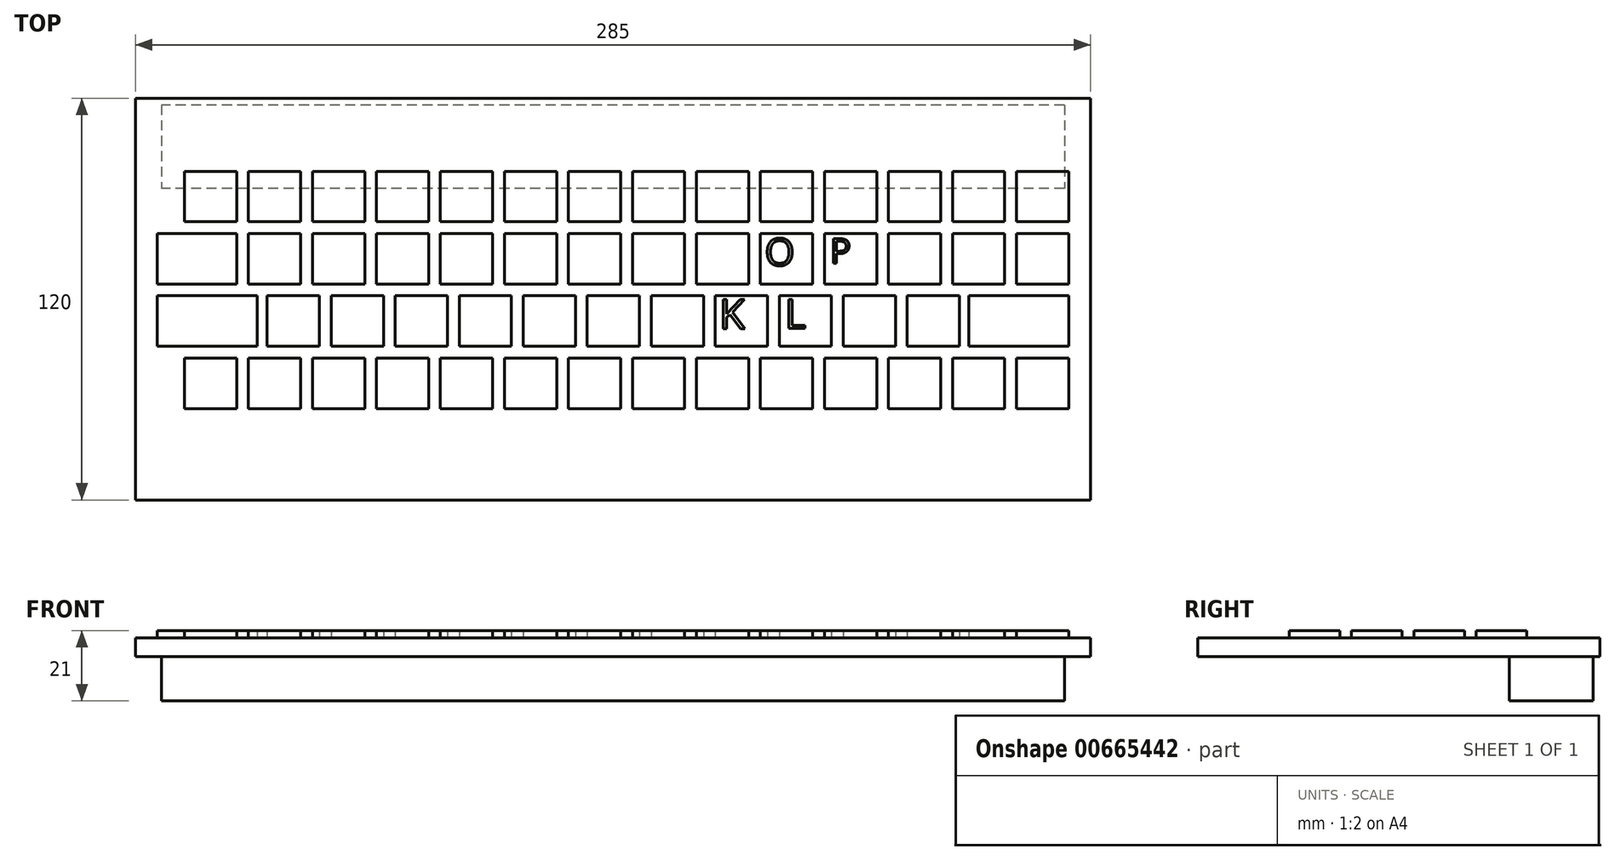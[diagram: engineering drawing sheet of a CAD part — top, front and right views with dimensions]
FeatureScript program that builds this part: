
annotation { "Feature Type Name" : "Feature", "Feature Type Description" : "" }
export const myFeature = defineFeature(function(context is Context, id is Id, definition is map)
    precondition{}
    {
        {
            var Q0;
            Q0=qCreatedBy(makeId("Top.planeOp"),FACE);
            var sketch = newSketch(context, id + "F0", { "sketchPlane" : qUnion([Q0])});
            skLineSegment(sketch, "E0.bottom", {"start": v(142.5, 60) * mm, "end": v(-142.5, 60) * mm});
            skLineSegment(sketch, "E0.top", {"start": v(142.5, -60) * mm, "end": v(-142.5, -60) * mm});
            skLineSegment(sketch, "E0.left", {"start": v(142.5, 60) * mm, "end": v(142.5, -60) * mm});
            skLineSegment(sketch, "E0.right", {"start": v(-142.5, 60) * mm, "end": v(-142.5, -60) * mm});
            skSolve(sketch);
        }
        {
            var Q0;
            Q0=makeQuery(id+"F0.imprint","IMPRINT",FACE,{"disambiguationData":[TD([[makeQuery(id+"F0.imprint","IMPRINT",EDGE,{"derivedFrom":sQuery(id+"F0.wireOp",EDGE,"E0.bottom")}),1.0]])]});
            extrude(context, id + "F1", {"entities" : qUnion([Q0]), "oppositeDirection" : true, "depth" : 5.6 * mm, "offsetDistance" : 25 * mm});
        }
        {
            var Q0;
            Q0=makeQuery(id+"F1.opExtrude","CAP_FACE",FACE,{"disambiguationData":[OSD([sQuery(id+"F0.wireOp",EDGE,"E0.bottom"),sQuery(id+"F0.wireOp",EDGE,"E0.top"),sQuery(id+"F0.wireOp",EDGE,"E0.left"),sQuery(id+"F0.wireOp",EDGE,"E0.right")])],"isStart":true});
            var sketch = newSketch(context, id + "F2", { "sketchPlane" : qUnion([Q0])});
            skLineSegment(sketch, "E1.0.1.0", {"start": v(136, 23.1) * mm, "end": v(120.4, 23.1) * mm});
            skLineSegment(sketch, "E1.0.1.1", {"start": v(120.4, 23.1) * mm, "end": v(120.4, 38.2) * mm});
            skLineSegment(sketch, "E1.0.1.2", {"start": v(136, 23.1) * mm, "end": v(136, 38.2) * mm});
            skPoint(sketch, "E1.0.1.3", {"position": v(128.2, 30.65) * mm});
            skLineSegment(sketch, "E1.0.1.4", {"start": v(136, 38.2) * mm, "end": v(120.4, 38.2) * mm});
            skLineSegment(sketch, "E2.0.1.0", {"start": v(136, 4.5) * mm, "end": v(120.4, 4.5) * mm});
            skLineSegment(sketch, "E2.0.1.1", {"start": v(136, 4.5) * mm, "end": v(136, 19.6) * mm});
            skLineSegment(sketch, "E2.0.1.2", {"start": v(120.4, 4.5) * mm, "end": v(120.4, 19.6) * mm});
            skPoint(sketch, "E2.0.1.3", {"position": v(128.2, 12.05) * mm});
            skLineSegment(sketch, "E2.0.1.4", {"start": v(136, 19.6) * mm, "end": v(120.4, 19.6) * mm});
            skLineSegment(sketch, "E2.0.2.0", {"start": v(136, -14.1) * mm, "end": v(106.2, -14.1) * mm});
            skLineSegment(sketch, "E2.0.2.1", {"start": v(136, -14.1) * mm, "end": v(136, 1) * mm});
            skLineSegment(sketch, "E2.0.2.2", {"start": v(106.2, -14.1) * mm, "end": v(106.2, 1) * mm});
            skPoint(sketch, "E2.0.2.3", {"position": v(115.4, -6.55) * mm});
            skLineSegment(sketch, "E2.0.2.4", {"start": v(136, 1) * mm, "end": v(106.2, 1) * mm});
            skLineSegment(sketch, "E2.0.3.0", {"start": v(136, -32.7) * mm, "end": v(120.4, -32.7) * mm});
            skLineSegment(sketch, "E2.0.3.1", {"start": v(136, -32.7) * mm, "end": v(136, -17.6) * mm});
            skLineSegment(sketch, "E2.0.3.2", {"start": v(120.4, -32.7) * mm, "end": v(120.4, -17.6) * mm});
            skPoint(sketch, "E2.0.3.3", {"position": v(128.2, -25.15) * mm});
            skLineSegment(sketch, "E2.0.3.4", {"start": v(136, -17.6) * mm, "end": v(120.4, -17.6) * mm});
            skLineSegment(sketch, "E2.1.0.0", {"start": v(116.9, 23.1) * mm, "end": v(101.3, 23.1) * mm});
            skLineSegment(sketch, "E2.1.0.1", {"start": v(116.9, 23.1) * mm, "end": v(116.9, 38.2) * mm});
            skLineSegment(sketch, "E2.1.0.2", {"start": v(101.3, 23.1) * mm, "end": v(101.3, 38.2) * mm});
            skPoint(sketch, "E2.1.0.3", {"position": v(109.1, 30.65) * mm});
            skLineSegment(sketch, "E2.1.0.4", {"start": v(116.9, 38.2) * mm, "end": v(101.3, 38.2) * mm});
            skLineSegment(sketch, "E2.1.1.0", {"start": v(116.9, 4.5) * mm, "end": v(101.3, 4.5) * mm});
            skLineSegment(sketch, "E2.1.1.1", {"start": v(116.9, 4.5) * mm, "end": v(116.9, 19.6) * mm});
            skLineSegment(sketch, "E2.1.1.2", {"start": v(101.3, 4.5) * mm, "end": v(101.3, 19.6) * mm});
            skPoint(sketch, "E2.1.1.3", {"position": v(109.1, 12.05) * mm});
            skLineSegment(sketch, "E2.1.1.4", {"start": v(116.9, 19.6) * mm, "end": v(101.3, 19.6) * mm});
            skLineSegment(sketch, "E2.1.3.0", {"start": v(116.9, -32.7) * mm, "end": v(101.3, -32.7) * mm});
            skLineSegment(sketch, "E2.1.3.1", {"start": v(116.9, -32.7) * mm, "end": v(116.9, -17.6) * mm});
            skLineSegment(sketch, "E2.1.3.2", {"start": v(101.3, -32.7) * mm, "end": v(101.3, -17.6) * mm});
            skPoint(sketch, "E2.1.3.3", {"position": v(109.1, -25.15) * mm});
            skLineSegment(sketch, "E2.1.3.4", {"start": v(116.9, -17.6) * mm, "end": v(101.3, -17.6) * mm});
            skLineSegment(sketch, "E2.2.0.0", {"start": v(97.8, 23.1) * mm, "end": v(82.2, 23.1) * mm});
            skLineSegment(sketch, "E2.2.0.1", {"start": v(97.8, 23.1) * mm, "end": v(97.8, 38.2) * mm});
            skLineSegment(sketch, "E2.2.0.2", {"start": v(82.2, 23.1) * mm, "end": v(82.2, 38.2) * mm});
            skPoint(sketch, "E2.2.0.3", {"position": v(90, 30.65) * mm});
            skLineSegment(sketch, "E2.2.0.4", {"start": v(97.8, 38.2) * mm, "end": v(82.2, 38.2) * mm});
            skLineSegment(sketch, "E2.2.1.0", {"start": v(97.8, 4.5) * mm, "end": v(82.2, 4.5) * mm});
            skLineSegment(sketch, "E2.2.1.1", {"start": v(97.8, 4.5) * mm, "end": v(97.8, 19.6) * mm});
            skLineSegment(sketch, "E2.2.1.2", {"start": v(82.2, 4.5) * mm, "end": v(82.2, 19.6) * mm});
            skPoint(sketch, "E2.2.1.3", {"position": v(90, 12.05) * mm});
            skLineSegment(sketch, "E2.2.1.4", {"start": v(97.8, 19.6) * mm, "end": v(82.2, 19.6) * mm});
            skLineSegment(sketch, "E2.2.2.0", {"start": v(103.4, -14.1) * mm, "end": v(87.8, -14.1) * mm});
            skLineSegment(sketch, "E2.2.2.1", {"start": v(103.4, -14.1) * mm, "end": v(103.4, 1) * mm});
            skLineSegment(sketch, "E2.2.2.2", {"start": v(87.8, -14.1) * mm, "end": v(87.8, 1) * mm});
            skPoint(sketch, "E2.2.2.3", {"position": v(95.6, -6.55) * mm});
            skLineSegment(sketch, "E2.2.2.4", {"start": v(103.4, 1) * mm, "end": v(87.8, 1) * mm});
            skLineSegment(sketch, "E2.2.3.0", {"start": v(97.8, -32.7) * mm, "end": v(82.2, -32.7) * mm});
            skLineSegment(sketch, "E2.2.3.1", {"start": v(97.8, -32.7) * mm, "end": v(97.8, -17.6) * mm});
            skLineSegment(sketch, "E2.2.3.2", {"start": v(82.2, -32.7) * mm, "end": v(82.2, -17.6) * mm});
            skPoint(sketch, "E2.2.3.3", {"position": v(90, -25.15) * mm});
            skLineSegment(sketch, "E2.2.3.4", {"start": v(97.8, -17.6) * mm, "end": v(82.2, -17.6) * mm});
            skLineSegment(sketch, "E2.3.0.0", {"start": v(78.7, 23.1) * mm, "end": v(63.1, 23.1) * mm});
            skLineSegment(sketch, "E2.3.0.1", {"start": v(78.7, 23.1) * mm, "end": v(78.7, 38.2) * mm});
            skLineSegment(sketch, "E2.3.0.2", {"start": v(63.1, 23.1) * mm, "end": v(63.1, 38.2) * mm});
            skPoint(sketch, "E2.3.0.3", {"position": v(70.9, 30.65) * mm});
            skLineSegment(sketch, "E2.3.0.4", {"start": v(78.7, 38.2) * mm, "end": v(63.1, 38.2) * mm});
            skLineSegment(sketch, "E2.3.1.0", {"start": v(78.7, 4.5) * mm, "end": v(63.1, 4.5) * mm});
            skLineSegment(sketch, "E2.3.1.1", {"start": v(78.7, 4.5) * mm, "end": v(78.7, 19.6) * mm});
            skLineSegment(sketch, "E2.3.1.2", {"start": v(63.1, 4.5) * mm, "end": v(63.1, 19.6) * mm});
            skPoint(sketch, "E2.3.1.3", {"position": v(70.9, 12.05) * mm});
            skLineSegment(sketch, "E2.3.1.4", {"start": v(78.7, 19.6) * mm, "end": v(63.1, 19.6) * mm});
            skLineSegment(sketch, "E2.3.2.0", {"start": v(84.3, -14.1) * mm, "end": v(68.7, -14.1) * mm});
            skLineSegment(sketch, "E2.3.2.1", {"start": v(84.3, -14.1) * mm, "end": v(84.3, 1) * mm});
            skLineSegment(sketch, "E2.3.2.2", {"start": v(68.7, -14.1) * mm, "end": v(68.7, 1) * mm});
            skPoint(sketch, "E2.3.2.3", {"position": v(76.5, -6.55) * mm});
            skLineSegment(sketch, "E2.3.2.4", {"start": v(84.3, 1) * mm, "end": v(68.7, 1) * mm});
            skLineSegment(sketch, "E2.3.3.0", {"start": v(78.7, -32.7) * mm, "end": v(63.1, -32.7) * mm});
            skLineSegment(sketch, "E2.3.3.1", {"start": v(78.7, -32.7) * mm, "end": v(78.7, -17.6) * mm});
            skLineSegment(sketch, "E2.3.3.2", {"start": v(63.1, -32.7) * mm, "end": v(63.1, -17.6) * mm});
            skPoint(sketch, "E2.3.3.3", {"position": v(70.9, -25.15) * mm});
            skLineSegment(sketch, "E2.3.3.4", {"start": v(78.7, -17.6) * mm, "end": v(63.1, -17.6) * mm});
            skLineSegment(sketch, "E2.4.0.0", {"start": v(59.6, 23.1) * mm, "end": v(44, 23.1) * mm});
            skLineSegment(sketch, "E2.4.0.1", {"start": v(59.6, 23.1) * mm, "end": v(59.6, 38.2) * mm});
            skLineSegment(sketch, "E2.4.0.2", {"start": v(44, 23.1) * mm, "end": v(44, 38.2) * mm});
            skPoint(sketch, "E2.4.0.3", {"position": v(51.8, 30.65) * mm});
            skLineSegment(sketch, "E2.4.0.4", {"start": v(59.6, 38.2) * mm, "end": v(44, 38.2) * mm});
            skLineSegment(sketch, "E2.4.1.0", {"start": v(59.6, 4.5) * mm, "end": v(44, 4.5) * mm});
            skLineSegment(sketch, "E2.4.1.1", {"start": v(59.6, 4.5) * mm, "end": v(59.6, 19.6) * mm});
            skLineSegment(sketch, "E2.4.1.2", {"start": v(44, 4.5) * mm, "end": v(44, 19.6) * mm});
            skPoint(sketch, "E2.4.1.3", {"position": v(51.8, 12.05) * mm});
            skLineSegment(sketch, "E2.4.1.4", {"start": v(59.6, 19.6) * mm, "end": v(44, 19.6) * mm});
            skLineSegment(sketch, "E2.4.2.0", {"start": v(65.2, -14.1) * mm, "end": v(49.6, -14.1) * mm});
            skLineSegment(sketch, "E2.4.2.1", {"start": v(65.2, -14.1) * mm, "end": v(65.2, 1) * mm});
            skLineSegment(sketch, "E2.4.2.2", {"start": v(49.6, -14.1) * mm, "end": v(49.6, 1) * mm});
            skPoint(sketch, "E2.4.2.3", {"position": v(57.4, -6.55) * mm});
            skLineSegment(sketch, "E2.4.2.4", {"start": v(65.2, 1) * mm, "end": v(49.6, 1) * mm});
            skLineSegment(sketch, "E2.4.3.0", {"start": v(59.6, -32.7) * mm, "end": v(44, -32.7) * mm});
            skLineSegment(sketch, "E2.4.3.1", {"start": v(59.6, -32.7) * mm, "end": v(59.6, -17.6) * mm});
            skLineSegment(sketch, "E2.4.3.2", {"start": v(44, -32.7) * mm, "end": v(44, -17.6) * mm});
            skPoint(sketch, "E2.4.3.3", {"position": v(51.8, -25.15) * mm});
            skLineSegment(sketch, "E2.4.3.4", {"start": v(59.6, -17.6) * mm, "end": v(44, -17.6) * mm});
            skLineSegment(sketch, "E2.5.0.0", {"start": v(40.5, 23.1) * mm, "end": v(24.9, 23.1) * mm});
            skLineSegment(sketch, "E2.5.0.1", {"start": v(40.5, 23.1) * mm, "end": v(40.5, 38.2) * mm});
            skLineSegment(sketch, "E2.5.0.2", {"start": v(24.9, 23.1) * mm, "end": v(24.9, 38.2) * mm});
            skPoint(sketch, "E2.5.0.3", {"position": v(32.7, 30.65) * mm});
            skLineSegment(sketch, "E2.5.0.4", {"start": v(40.5, 38.2) * mm, "end": v(24.9, 38.2) * mm});
            skLineSegment(sketch, "E2.5.1.0", {"start": v(40.5, 4.5) * mm, "end": v(24.9, 4.5) * mm});
            skLineSegment(sketch, "E2.5.1.1", {"start": v(40.5, 4.5) * mm, "end": v(40.5, 19.6) * mm});
            skLineSegment(sketch, "E2.5.1.2", {"start": v(24.9, 4.5) * mm, "end": v(24.9, 19.6) * mm});
            skPoint(sketch, "E2.5.1.3", {"position": v(32.7, 12.05) * mm});
            skLineSegment(sketch, "E2.5.1.4", {"start": v(40.5, 19.6) * mm, "end": v(24.9, 19.6) * mm});
            skLineSegment(sketch, "E2.5.2.0", {"start": v(46.1, -14.1) * mm, "end": v(30.5, -14.1) * mm});
            skLineSegment(sketch, "E2.5.2.1", {"start": v(46.1, -14.1) * mm, "end": v(46.1, 1) * mm});
            skLineSegment(sketch, "E2.5.2.2", {"start": v(30.5, -14.1) * mm, "end": v(30.5, 1) * mm});
            skPoint(sketch, "E2.5.2.3", {"position": v(38.3, -6.55) * mm});
            skLineSegment(sketch, "E2.5.2.4", {"start": v(46.1, 1) * mm, "end": v(30.5, 1) * mm});
            skLineSegment(sketch, "E2.5.3.0", {"start": v(40.5, -32.7) * mm, "end": v(24.9, -32.7) * mm});
            skLineSegment(sketch, "E2.5.3.1", {"start": v(40.5, -32.7) * mm, "end": v(40.5, -17.6) * mm});
            skLineSegment(sketch, "E2.5.3.2", {"start": v(24.9, -32.7) * mm, "end": v(24.9, -17.6) * mm});
            skPoint(sketch, "E2.5.3.3", {"position": v(32.7, -25.15) * mm});
            skLineSegment(sketch, "E2.5.3.4", {"start": v(40.5, -17.6) * mm, "end": v(24.9, -17.6) * mm});
            skLineSegment(sketch, "E2.6.0.0", {"start": v(21.4, 23.1) * mm, "end": v(5.8, 23.1) * mm});
            skLineSegment(sketch, "E2.6.0.1", {"start": v(21.4, 23.1) * mm, "end": v(21.4, 38.2) * mm});
            skLineSegment(sketch, "E2.6.0.2", {"start": v(5.8, 23.1) * mm, "end": v(5.8, 38.2) * mm});
            skPoint(sketch, "E2.6.0.3", {"position": v(13.6, 30.65) * mm});
            skLineSegment(sketch, "E2.6.0.4", {"start": v(21.4, 38.2) * mm, "end": v(5.8, 38.2) * mm});
            skLineSegment(sketch, "E2.6.1.0", {"start": v(21.4, 4.5) * mm, "end": v(5.8, 4.5) * mm});
            skLineSegment(sketch, "E2.6.1.1", {"start": v(21.4, 4.5) * mm, "end": v(21.4, 19.6) * mm});
            skLineSegment(sketch, "E2.6.1.2", {"start": v(5.8, 4.5) * mm, "end": v(5.8, 19.6) * mm});
            skPoint(sketch, "E2.6.1.3", {"position": v(13.6, 12.05) * mm});
            skLineSegment(sketch, "E2.6.1.4", {"start": v(21.4, 19.6) * mm, "end": v(5.8, 19.6) * mm});
            skLineSegment(sketch, "E2.6.2.0", {"start": v(27, -14.1) * mm, "end": v(11.4, -14.1) * mm});
            skLineSegment(sketch, "E2.6.2.1", {"start": v(27, -14.1) * mm, "end": v(27, 1) * mm});
            skLineSegment(sketch, "E2.6.2.2", {"start": v(11.4, -14.1) * mm, "end": v(11.4, 1) * mm});
            skPoint(sketch, "E2.6.2.3", {"position": v(19.2, -6.55) * mm});
            skLineSegment(sketch, "E2.6.2.4", {"start": v(27, 1) * mm, "end": v(11.4, 1) * mm});
            skLineSegment(sketch, "E2.6.3.0", {"start": v(21.4, -32.7) * mm, "end": v(5.8, -32.7) * mm});
            skLineSegment(sketch, "E2.6.3.1", {"start": v(21.4, -32.7) * mm, "end": v(21.4, -17.6) * mm});
            skLineSegment(sketch, "E2.6.3.2", {"start": v(5.8, -32.7) * mm, "end": v(5.8, -17.6) * mm});
            skPoint(sketch, "E2.6.3.3", {"position": v(13.6, -25.15) * mm});
            skLineSegment(sketch, "E2.6.3.4", {"start": v(21.4, -17.6) * mm, "end": v(5.8, -17.6) * mm});
            skLineSegment(sketch, "E2.7.0.0", {"start": v(2.3, 23.1) * mm, "end": v(-13.3, 23.1) * mm});
            skLineSegment(sketch, "E2.7.0.1", {"start": v(2.3, 23.1) * mm, "end": v(2.3, 38.2) * mm});
            skLineSegment(sketch, "E2.7.0.2", {"start": v(-13.3, 23.1) * mm, "end": v(-13.3, 38.2) * mm});
            skPoint(sketch, "E2.7.0.3", {"position": v(-5.5, 30.65) * mm});
            skLineSegment(sketch, "E2.7.0.4", {"start": v(2.3, 38.2) * mm, "end": v(-13.3, 38.2) * mm});
            skLineSegment(sketch, "E2.7.1.0", {"start": v(2.3, 4.5) * mm, "end": v(-13.3, 4.5) * mm});
            skLineSegment(sketch, "E2.7.1.1", {"start": v(2.3, 4.5) * mm, "end": v(2.3, 19.6) * mm});
            skLineSegment(sketch, "E2.7.1.2", {"start": v(-13.3, 4.5) * mm, "end": v(-13.3, 19.6) * mm});
            skPoint(sketch, "E2.7.1.3", {"position": v(-5.5, 12.05) * mm});
            skLineSegment(sketch, "E2.7.1.4", {"start": v(2.3, 19.6) * mm, "end": v(-13.3, 19.6) * mm});
            skLineSegment(sketch, "E2.7.2.0", {"start": v(7.9, -14.1) * mm, "end": v(-7.7, -14.1) * mm});
            skLineSegment(sketch, "E2.7.2.1", {"start": v(7.9, -14.1) * mm, "end": v(7.9, 1) * mm});
            skLineSegment(sketch, "E2.7.2.2", {"start": v(-7.7, -14.1) * mm, "end": v(-7.7, 1) * mm});
            skPoint(sketch, "E2.7.2.3", {"position": v(0.1, -6.55) * mm});
            skLineSegment(sketch, "E2.7.2.4", {"start": v(7.9, 1) * mm, "end": v(-7.7, 1) * mm});
            skLineSegment(sketch, "E2.7.3.0", {"start": v(2.3, -32.7) * mm, "end": v(-13.3, -32.7) * mm});
            skLineSegment(sketch, "E2.7.3.1", {"start": v(2.3, -32.7) * mm, "end": v(2.3, -17.6) * mm});
            skLineSegment(sketch, "E2.7.3.2", {"start": v(-13.3, -32.7) * mm, "end": v(-13.3, -17.6) * mm});
            skPoint(sketch, "E2.7.3.3", {"position": v(-5.5, -25.15) * mm});
            skLineSegment(sketch, "E2.7.3.4", {"start": v(2.3, -17.6) * mm, "end": v(-13.3, -17.6) * mm});
            skLineSegment(sketch, "E2.8.0.0", {"start": v(-16.8, 23.1) * mm, "end": v(-32.4, 23.1) * mm});
            skLineSegment(sketch, "E2.8.0.1", {"start": v(-16.8, 23.1) * mm, "end": v(-16.8, 38.2) * mm});
            skLineSegment(sketch, "E2.8.0.2", {"start": v(-32.4, 23.1) * mm, "end": v(-32.4, 38.2) * mm});
            skPoint(sketch, "E2.8.0.3", {"position": v(-24.6, 30.65) * mm});
            skLineSegment(sketch, "E2.8.0.4", {"start": v(-16.8, 38.2) * mm, "end": v(-32.4, 38.2) * mm});
            skLineSegment(sketch, "E2.8.1.0", {"start": v(-16.8, 4.5) * mm, "end": v(-32.4, 4.5) * mm});
            skLineSegment(sketch, "E2.8.1.1", {"start": v(-16.8, 4.5) * mm, "end": v(-16.8, 19.6) * mm});
            skLineSegment(sketch, "E2.8.1.2", {"start": v(-32.4, 4.5) * mm, "end": v(-32.4, 19.6) * mm});
            skPoint(sketch, "E2.8.1.3", {"position": v(-24.6, 12.05) * mm});
            skLineSegment(sketch, "E2.8.1.4", {"start": v(-16.8, 19.6) * mm, "end": v(-32.4, 19.6) * mm});
            skLineSegment(sketch, "E2.8.2.0", {"start": v(-11.2, -14.1) * mm, "end": v(-26.8, -14.1) * mm});
            skLineSegment(sketch, "E2.8.2.1", {"start": v(-11.2, -14.1) * mm, "end": v(-11.2, 1) * mm});
            skLineSegment(sketch, "E2.8.2.2", {"start": v(-26.8, -14.1) * mm, "end": v(-26.8, 1) * mm});
            skPoint(sketch, "E2.8.2.3", {"position": v(-19, -6.55) * mm});
            skLineSegment(sketch, "E2.8.2.4", {"start": v(-11.2, 1) * mm, "end": v(-26.8, 1) * mm});
            skLineSegment(sketch, "E2.8.3.0", {"start": v(-16.8, -32.7) * mm, "end": v(-32.4, -32.7) * mm});
            skLineSegment(sketch, "E2.8.3.1", {"start": v(-16.8, -32.7) * mm, "end": v(-16.8, -17.6) * mm});
            skLineSegment(sketch, "E2.8.3.2", {"start": v(-32.4, -32.7) * mm, "end": v(-32.4, -17.6) * mm});
            skPoint(sketch, "E2.8.3.3", {"position": v(-24.6, -25.15) * mm});
            skLineSegment(sketch, "E2.8.3.4", {"start": v(-16.8, -17.6) * mm, "end": v(-32.4, -17.6) * mm});
            skLineSegment(sketch, "E2.9.0.0", {"start": v(-35.9, 23.1) * mm, "end": v(-51.5, 23.1) * mm});
            skLineSegment(sketch, "E2.9.0.1", {"start": v(-35.9, 23.1) * mm, "end": v(-35.9, 38.2) * mm});
            skLineSegment(sketch, "E2.9.0.2", {"start": v(-51.5, 23.1) * mm, "end": v(-51.5, 38.2) * mm});
            skPoint(sketch, "E2.9.0.3", {"position": v(-43.7, 30.65) * mm});
            skLineSegment(sketch, "E2.9.0.4", {"start": v(-35.9, 38.2) * mm, "end": v(-51.5, 38.2) * mm});
            skLineSegment(sketch, "E2.9.1.0", {"start": v(-35.9, 4.5) * mm, "end": v(-51.5, 4.5) * mm});
            skLineSegment(sketch, "E2.9.1.1", {"start": v(-35.9, 4.5) * mm, "end": v(-35.9, 19.6) * mm});
            skLineSegment(sketch, "E2.9.1.2", {"start": v(-51.5, 4.5) * mm, "end": v(-51.5, 19.6) * mm});
            skPoint(sketch, "E2.9.1.3", {"position": v(-43.7, 12.05) * mm});
            skLineSegment(sketch, "E2.9.1.4", {"start": v(-35.9, 19.6) * mm, "end": v(-51.5, 19.6) * mm});
            skLineSegment(sketch, "E2.9.2.0", {"start": v(-30.3, -14.1) * mm, "end": v(-45.9, -14.1) * mm});
            skLineSegment(sketch, "E2.9.2.1", {"start": v(-30.3, -14.1) * mm, "end": v(-30.3, 1) * mm});
            skLineSegment(sketch, "E2.9.2.2", {"start": v(-45.9, -14.1) * mm, "end": v(-45.9, 1) * mm});
            skPoint(sketch, "E2.9.2.3", {"position": v(-38.1, -6.55) * mm});
            skLineSegment(sketch, "E2.9.2.4", {"start": v(-30.3, 1) * mm, "end": v(-45.9, 1) * mm});
            skLineSegment(sketch, "E2.9.3.0", {"start": v(-35.9, -32.7) * mm, "end": v(-51.5, -32.7) * mm});
            skLineSegment(sketch, "E2.9.3.1", {"start": v(-35.9, -32.7) * mm, "end": v(-35.9, -17.6) * mm});
            skLineSegment(sketch, "E2.9.3.2", {"start": v(-51.5, -32.7) * mm, "end": v(-51.5, -17.6) * mm});
            skPoint(sketch, "E2.9.3.3", {"position": v(-43.7, -25.15) * mm});
            skLineSegment(sketch, "E2.9.3.4", {"start": v(-35.9, -17.6) * mm, "end": v(-51.5, -17.6) * mm});
            skLineSegment(sketch, "E2.10.0.0", {"start": v(-55, 23.1) * mm, "end": v(-70.6, 23.1) * mm});
            skLineSegment(sketch, "E2.10.0.1", {"start": v(-55, 23.1) * mm, "end": v(-55, 38.2) * mm});
            skLineSegment(sketch, "E2.10.0.2", {"start": v(-70.6, 23.1) * mm, "end": v(-70.6, 38.2) * mm});
            skPoint(sketch, "E2.10.0.3", {"position": v(-62.8, 30.65) * mm});
            skLineSegment(sketch, "E2.10.0.4", {"start": v(-55, 38.2) * mm, "end": v(-70.6, 38.2) * mm});
            skLineSegment(sketch, "E2.10.1.0", {"start": v(-55, 4.5) * mm, "end": v(-70.6, 4.5) * mm});
            skLineSegment(sketch, "E2.10.1.1", {"start": v(-55, 4.5) * mm, "end": v(-55, 19.6) * mm});
            skLineSegment(sketch, "E2.10.1.2", {"start": v(-70.6, 4.5) * mm, "end": v(-70.6, 19.6) * mm});
            skPoint(sketch, "E2.10.1.3", {"position": v(-62.8, 12.05) * mm});
            skLineSegment(sketch, "E2.10.1.4", {"start": v(-55, 19.6) * mm, "end": v(-70.6, 19.6) * mm});
            skLineSegment(sketch, "E2.10.2.0", {"start": v(-49.4, -14.1) * mm, "end": v(-65, -14.1) * mm});
            skLineSegment(sketch, "E2.10.2.1", {"start": v(-49.4, -14.1) * mm, "end": v(-49.4, 1) * mm});
            skLineSegment(sketch, "E2.10.2.2", {"start": v(-65, -14.1) * mm, "end": v(-65, 1) * mm});
            skPoint(sketch, "E2.10.2.3", {"position": v(-57.2, -6.55) * mm});
            skLineSegment(sketch, "E2.10.2.4", {"start": v(-49.4, 1) * mm, "end": v(-65, 1) * mm});
            skLineSegment(sketch, "E2.10.3.0", {"start": v(-55, -32.7) * mm, "end": v(-70.6, -32.7) * mm});
            skLineSegment(sketch, "E2.10.3.1", {"start": v(-55, -32.7) * mm, "end": v(-55, -17.6) * mm});
            skLineSegment(sketch, "E2.10.3.2", {"start": v(-70.6, -32.7) * mm, "end": v(-70.6, -17.6) * mm});
            skPoint(sketch, "E2.10.3.3", {"position": v(-62.8, -25.15) * mm});
            skLineSegment(sketch, "E2.10.3.4", {"start": v(-55, -17.6) * mm, "end": v(-70.6, -17.6) * mm});
            skLineSegment(sketch, "E2.11.0.0", {"start": v(-74.1, 23.1) * mm, "end": v(-89.7, 23.1) * mm});
            skLineSegment(sketch, "E2.11.0.1", {"start": v(-74.1, 23.1) * mm, "end": v(-74.1, 38.2) * mm});
            skLineSegment(sketch, "E2.11.0.2", {"start": v(-89.7, 23.1) * mm, "end": v(-89.7, 38.2) * mm});
            skPoint(sketch, "E2.11.0.3", {"position": v(-81.9, 30.65) * mm});
            skLineSegment(sketch, "E2.11.0.4", {"start": v(-74.1, 38.2) * mm, "end": v(-89.7, 38.2) * mm});
            skLineSegment(sketch, "E2.11.1.0", {"start": v(-74.1, 4.5) * mm, "end": v(-89.7, 4.5) * mm});
            skLineSegment(sketch, "E2.11.1.1", {"start": v(-74.1, 4.5) * mm, "end": v(-74.1, 19.6) * mm});
            skLineSegment(sketch, "E2.11.1.2", {"start": v(-89.7, 4.5) * mm, "end": v(-89.7, 19.6) * mm});
            skPoint(sketch, "E2.11.1.3", {"position": v(-81.9, 12.05) * mm});
            skLineSegment(sketch, "E2.11.1.4", {"start": v(-74.1, 19.6) * mm, "end": v(-89.7, 19.6) * mm});
            skLineSegment(sketch, "E2.11.2.0", {"start": v(-68.5, -14.1) * mm, "end": v(-84.1, -14.1) * mm});
            skLineSegment(sketch, "E2.11.2.1", {"start": v(-68.5, -14.1) * mm, "end": v(-68.5, 1) * mm});
            skLineSegment(sketch, "E2.11.2.2", {"start": v(-84.1, -14.1) * mm, "end": v(-84.1, 1) * mm});
            skPoint(sketch, "E2.11.2.3", {"position": v(-76.3, -6.55) * mm});
            skLineSegment(sketch, "E2.11.2.4", {"start": v(-68.5, 1) * mm, "end": v(-84.1, 1) * mm});
            skLineSegment(sketch, "E2.11.3.0", {"start": v(-74.1, -32.7) * mm, "end": v(-89.7, -32.7) * mm});
            skLineSegment(sketch, "E2.11.3.1", {"start": v(-74.1, -32.7) * mm, "end": v(-74.1, -17.6) * mm});
            skLineSegment(sketch, "E2.11.3.2", {"start": v(-89.7, -32.7) * mm, "end": v(-89.7, -17.6) * mm});
            skPoint(sketch, "E2.11.3.3", {"position": v(-81.9, -25.15) * mm});
            skLineSegment(sketch, "E2.11.3.4", {"start": v(-74.1, -17.6) * mm, "end": v(-89.7, -17.6) * mm});
            skLineSegment(sketch, "E2.12.0.0", {"start": v(-93.2, 23.1) * mm, "end": v(-108.8, 23.1) * mm});
            skLineSegment(sketch, "E2.12.0.1", {"start": v(-93.2, 23.1) * mm, "end": v(-93.2, 38.2) * mm});
            skLineSegment(sketch, "E2.12.0.2", {"start": v(-108.8, 23.1) * mm, "end": v(-108.8, 38.2) * mm});
            skPoint(sketch, "E2.12.0.3", {"position": v(-101, 30.65) * mm});
            skLineSegment(sketch, "E2.12.0.4", {"start": v(-93.2, 38.2) * mm, "end": v(-108.8, 38.2) * mm});
            skLineSegment(sketch, "E2.12.1.0", {"start": v(-93.2, 4.5) * mm, "end": v(-108.8, 4.5) * mm});
            skLineSegment(sketch, "E2.12.1.1", {"start": v(-93.2, 4.5) * mm, "end": v(-93.2, 19.6) * mm});
            skLineSegment(sketch, "E2.12.1.2", {"start": v(-108.8, 4.5) * mm, "end": v(-108.8, 19.6) * mm});
            skPoint(sketch, "E2.12.1.3", {"position": v(-101, 12.05) * mm});
            skLineSegment(sketch, "E2.12.1.4", {"start": v(-93.2, 19.6) * mm, "end": v(-108.8, 19.6) * mm});
            skLineSegment(sketch, "E2.12.2.0", {"start": v(-87.6, -14.1) * mm, "end": v(-103.2, -14.1) * mm});
            skLineSegment(sketch, "E2.12.2.1", {"start": v(-87.6, -14.1) * mm, "end": v(-87.6, 1) * mm});
            skLineSegment(sketch, "E2.12.2.2", {"start": v(-103.2, -14.1) * mm, "end": v(-103.2, 1) * mm});
            skPoint(sketch, "E2.12.2.3", {"position": v(-95.4, -6.55) * mm});
            skLineSegment(sketch, "E2.12.2.4", {"start": v(-87.6, 1) * mm, "end": v(-103.2, 1) * mm});
            skLineSegment(sketch, "E2.12.3.0", {"start": v(-93.2, -32.7) * mm, "end": v(-108.8, -32.7) * mm});
            skLineSegment(sketch, "E2.12.3.1", {"start": v(-93.2, -32.7) * mm, "end": v(-93.2, -17.6) * mm});
            skLineSegment(sketch, "E2.12.3.2", {"start": v(-108.8, -32.7) * mm, "end": v(-108.8, -17.6) * mm});
            skPoint(sketch, "E2.12.3.3", {"position": v(-101, -25.15) * mm});
            skLineSegment(sketch, "E2.12.3.4", {"start": v(-93.2, -17.6) * mm, "end": v(-108.8, -17.6) * mm});
            skLineSegment(sketch, "E2.13.0.0", {"start": v(-112.3, 23.1) * mm, "end": v(-127.9, 23.1) * mm});
            skLineSegment(sketch, "E2.13.0.1", {"start": v(-112.3, 23.1) * mm, "end": v(-112.3, 38.2) * mm});
            skLineSegment(sketch, "E2.13.0.2", {"start": v(-127.9, 23.1) * mm, "end": v(-127.9, 38.2) * mm});
            skPoint(sketch, "E2.13.0.3", {"position": v(-120.1, 30.65) * mm});
            skLineSegment(sketch, "E2.13.0.4", {"start": v(-112.3, 38.2) * mm, "end": v(-127.9, 38.2) * mm});
            skLineSegment(sketch, "E2.13.1.0", {"start": v(-112.3, 4.5) * mm, "end": v(-136, 4.5) * mm});
            skLineSegment(sketch, "E2.13.1.1", {"start": v(-112.3, 4.5) * mm, "end": v(-112.3, 19.6) * mm});
            skLineSegment(sketch, "E2.13.1.2", {"start": v(-136, 4.5) * mm, "end": v(-136, 19.6) * mm});
            skPoint(sketch, "E2.13.1.3", {"position": v(-127.7, 12.05) * mm});
            skLineSegment(sketch, "E2.13.1.4", {"start": v(-112.3, 19.6) * mm, "end": v(-136, 19.6) * mm});
            skLineSegment(sketch, "E2.13.2.0", {"start": v(-106.2, -14.1) * mm, "end": v(-136, -14.1) * mm});
            skLineSegment(sketch, "E2.13.2.1", {"start": v(-106.2, -14.1) * mm, "end": v(-106.2, 1) * mm});
            skLineSegment(sketch, "E2.13.2.2", {"start": v(-136, -14.1) * mm, "end": v(-136, 1) * mm});
            skPoint(sketch, "E2.13.2.3", {"position": v(-120.1, -6.55) * mm});
            skLineSegment(sketch, "E2.13.2.4", {"start": v(-106.2, 1) * mm, "end": v(-136, 1) * mm});
            skLineSegment(sketch, "E2.13.3.0", {"start": v(-112.3, -32.7) * mm, "end": v(-127.9, -32.7) * mm});
            skLineSegment(sketch, "E2.13.3.1", {"start": v(-112.3, -32.7) * mm, "end": v(-112.3, -17.6) * mm});
            skLineSegment(sketch, "E2.13.3.2", {"start": v(-127.9, -32.7) * mm, "end": v(-127.9, -17.6) * mm});
            skPoint(sketch, "E2.13.3.3", {"position": v(-120.1, -25.15) * mm});
            skLineSegment(sketch, "E2.13.3.4", {"start": v(-112.3, -17.6) * mm, "end": v(-127.9, -17.6) * mm});
            skLineSegment(sketch, "E2.direction1", {"start": v(120.4, 23.1) * mm, "end": v(101.3, 23.1) * mm, "construction": true});
            skLineSegment(sketch, "E2.direction2", {"start": v(120.4, 23.1) * mm, "end": v(120.4, 4.5) * mm, "construction": true});
            skSolve(sketch);
        }
        {
            var Q0;
            Q0=makeQuery(id+"F2.imprint","IMPRINT",FACE,{"disambiguationData":[TD([[makeQuery(id+"F2.imprint","IMPRINT",EDGE,{"derivedFrom":sQuery(id+"F2.wireOp",EDGE,"E2.13.0.0")}),-1.0]])]});
            var Q1;
            Q1=makeQuery(id+"F2.imprint","IMPRINT",FACE,{"disambiguationData":[TD([[makeQuery(id+"F2.imprint","IMPRINT",EDGE,{"derivedFrom":sQuery(id+"F2.wireOp",EDGE,"E2.13.1.0")}),-1.0]])]});
            var Q2;
            Q2=makeQuery(id+"F2.imprint","IMPRINT",FACE,{"disambiguationData":[TD([[makeQuery(id+"F2.imprint","IMPRINT",EDGE,{"derivedFrom":sQuery(id+"F2.wireOp",EDGE,"E2.13.2.0")}),-1.0]])]});
            var Q3;
            Q3=makeQuery(id+"F2.imprint","IMPRINT",FACE,{"disambiguationData":[TD([[makeQuery(id+"F2.imprint","IMPRINT",EDGE,{"derivedFrom":sQuery(id+"F2.wireOp",EDGE,"E2.12.1.0")}),-1.0]])]});
            var Q4;
            Q4=makeQuery(id+"F2.imprint","IMPRINT",FACE,{"disambiguationData":[TD([[makeQuery(id+"F2.imprint","IMPRINT",EDGE,{"derivedFrom":sQuery(id+"F2.wireOp",EDGE,"E2.12.0.0")}),-1.0]])]});
            var Q5;
            Q5=makeQuery(id+"F2.imprint","IMPRINT",FACE,{"disambiguationData":[TD([[makeQuery(id+"F2.imprint","IMPRINT",EDGE,{"derivedFrom":sQuery(id+"F2.wireOp",EDGE,"E2.9.2.0")}),-1.0]])]});
            var Q6;
            Q6=makeQuery(id+"F2.imprint","IMPRINT",FACE,{"disambiguationData":[TD([[makeQuery(id+"F2.imprint","IMPRINT",EDGE,{"derivedFrom":sQuery(id+"F2.wireOp",EDGE,"E2.5.2.0")}),-1.0]])]});
            var Q7;
            Q7=makeQuery(id+"F2.imprint","IMPRINT",FACE,{"disambiguationData":[TD([[makeQuery(id+"F2.imprint","IMPRINT",EDGE,{"derivedFrom":sQuery(id+"F2.wireOp",EDGE,"E2.4.2.0")}),-1.0]])]});
            var Q8;
            Q8=makeQuery(id+"F2.imprint","IMPRINT",FACE,{"disambiguationData":[TD([[makeQuery(id+"F2.imprint","IMPRINT",EDGE,{"derivedFrom":sQuery(id+"F2.wireOp",EDGE,"E2.5.1.0")}),-1.0]])]});
            var Q9;
            Q9=makeQuery(id+"F2.imprint","IMPRINT",FACE,{"disambiguationData":[TD([[makeQuery(id+"F2.imprint","IMPRINT",EDGE,{"derivedFrom":sQuery(id+"F2.wireOp",EDGE,"E2.8.3.0")}),-1.0]])]});
            var Q10;
            Q10=makeQuery(id+"F2.imprint","IMPRINT",FACE,{"disambiguationData":[TD([[makeQuery(id+"F2.imprint","IMPRINT",EDGE,{"derivedFrom":sQuery(id+"F2.wireOp",EDGE,"E2.4.3.0")}),-1.0]])]});
            var Q11;
            Q11=makeQuery(id+"F2.imprint","IMPRINT",FACE,{"disambiguationData":[TD([[makeQuery(id+"F2.imprint","IMPRINT",EDGE,{"derivedFrom":sQuery(id+"F2.wireOp",EDGE,"E2.4.0.0")}),-1.0]])]});
            var Q12;
            Q12=makeQuery(id+"F2.imprint","IMPRINT",FACE,{"disambiguationData":[TD([[makeQuery(id+"F2.imprint","IMPRINT",EDGE,{"derivedFrom":sQuery(id+"F2.wireOp",EDGE,"E2.3.2.0")}),-1.0]])]});
            var Q13;
            Q13=makeQuery(id+"F2.imprint","IMPRINT",FACE,{"disambiguationData":[TD([[makeQuery(id+"F2.imprint","IMPRINT",EDGE,{"derivedFrom":sQuery(id+"F2.wireOp",EDGE,"E2.11.0.0")}),-1.0]])]});
            var Q14;
            Q14=makeQuery(id+"F2.imprint","IMPRINT",FACE,{"disambiguationData":[TD([[makeQuery(id+"F2.imprint","IMPRINT",EDGE,{"derivedFrom":sQuery(id+"F2.wireOp",EDGE,"E2.3.3.0")}),-1.0]])]});
            var Q15;
            Q15=makeQuery(id+"F2.imprint","IMPRINT",FACE,{"disambiguationData":[TD([[makeQuery(id+"F2.imprint","IMPRINT",EDGE,{"derivedFrom":sQuery(id+"F2.wireOp",EDGE,"E1.0.1.0")}),-1.0]])]});
            var Q16;
            Q16=makeQuery(id+"F2.imprint","IMPRINT",FACE,{"disambiguationData":[TD([[makeQuery(id+"F2.imprint","IMPRINT",EDGE,{"derivedFrom":sQuery(id+"F2.wireOp",EDGE,"E2.0.1.0")}),-1.0]])]});
            var Q17;
            Q17=makeQuery(id+"F2.imprint","IMPRINT",FACE,{"disambiguationData":[TD([[makeQuery(id+"F2.imprint","IMPRINT",EDGE,{"derivedFrom":sQuery(id+"F2.wireOp",EDGE,"E2.7.0.0")}),-1.0]])]});
            var Q18;
            Q18=makeQuery(id+"F2.imprint","IMPRINT",FACE,{"disambiguationData":[TD([[makeQuery(id+"F2.imprint","IMPRINT",EDGE,{"derivedFrom":sQuery(id+"F2.wireOp",EDGE,"E2.0.2.0")}),-1.0]])]});
            var Q19;
            Q19=makeQuery(id+"F2.imprint","IMPRINT",FACE,{"disambiguationData":[TD([[makeQuery(id+"F2.imprint","IMPRINT",EDGE,{"derivedFrom":sQuery(id+"F2.wireOp",EDGE,"E2.0.3.0")}),-1.0]])]});
            var Q20;
            Q20=makeQuery(id+"F2.imprint","IMPRINT",FACE,{"disambiguationData":[TD([[makeQuery(id+"F2.imprint","IMPRINT",EDGE,{"derivedFrom":sQuery(id+"F2.wireOp",EDGE,"E2.1.0.0")}),-1.0]])]});
            var Q21;
            Q21=makeQuery(id+"F2.imprint","IMPRINT",FACE,{"disambiguationData":[TD([[makeQuery(id+"F2.imprint","IMPRINT",EDGE,{"derivedFrom":sQuery(id+"F2.wireOp",EDGE,"E2.1.1.0")}),-1.0]])]});
            var Q22;
            Q22=makeQuery(id+"F2.imprint","IMPRINT",FACE,{"disambiguationData":[TD([[makeQuery(id+"F2.imprint","IMPRINT",EDGE,{"derivedFrom":sQuery(id+"F2.wireOp",EDGE,"E2.7.3.0")}),-1.0]])]});
            var Q23;
            Q23=makeQuery(id+"F2.imprint","IMPRINT",FACE,{"disambiguationData":[TD([[makeQuery(id+"F2.imprint","IMPRINT",EDGE,{"derivedFrom":sQuery(id+"F2.wireOp",EDGE,"E2.11.3.0")}),-1.0]])]});
            var Q24;
            Q24=makeQuery(id+"F2.imprint","IMPRINT",FACE,{"disambiguationData":[TD([[makeQuery(id+"F2.imprint","IMPRINT",EDGE,{"derivedFrom":sQuery(id+"F2.wireOp",EDGE,"E2.8.2.0")}),-1.0]])]});
            var Q25;
            Q25=makeQuery(id+"F2.imprint","IMPRINT",FACE,{"disambiguationData":[TD([[makeQuery(id+"F2.imprint","IMPRINT",EDGE,{"derivedFrom":sQuery(id+"F2.wireOp",EDGE,"E2.10.0.0")}),-1.0]])]});
            var Q26;
            Q26=makeQuery(id+"F2.imprint","IMPRINT",FACE,{"disambiguationData":[TD([[makeQuery(id+"F2.imprint","IMPRINT",EDGE,{"derivedFrom":sQuery(id+"F2.wireOp",EDGE,"E2.6.0.0")}),-1.0]])]});
            var Q27;
            Q27=makeQuery(id+"F2.imprint","IMPRINT",FACE,{"disambiguationData":[TD([[makeQuery(id+"F2.imprint","IMPRINT",EDGE,{"derivedFrom":sQuery(id+"F2.wireOp",EDGE,"E2.6.2.0")}),-1.0]])]});
            var Q28;
            Q28=makeQuery(id+"F2.imprint","IMPRINT",FACE,{"disambiguationData":[TD([[makeQuery(id+"F2.imprint","IMPRINT",EDGE,{"derivedFrom":sQuery(id+"F2.wireOp",EDGE,"E2.9.0.0")}),-1.0]])]});
            var Q29;
            Q29=makeQuery(id+"F2.imprint","IMPRINT",FACE,{"disambiguationData":[TD([[makeQuery(id+"F2.imprint","IMPRINT",EDGE,{"derivedFrom":sQuery(id+"F2.wireOp",EDGE,"E2.2.3.0")}),-1.0]])]});
            var Q30;
            Q30=makeQuery(id+"F2.imprint","IMPRINT",FACE,{"disambiguationData":[TD([[makeQuery(id+"F2.imprint","IMPRINT",EDGE,{"derivedFrom":sQuery(id+"F2.wireOp",EDGE,"E2.3.0.0")}),-1.0]])]});
            var Q31;
            Q31=makeQuery(id+"F2.imprint","IMPRINT",FACE,{"disambiguationData":[TD([[makeQuery(id+"F2.imprint","IMPRINT",EDGE,{"derivedFrom":sQuery(id+"F2.wireOp",EDGE,"E2.2.2.0")}),-1.0]])]});
            var Q32;
            Q32=makeQuery(id+"F2.imprint","IMPRINT",FACE,{"disambiguationData":[TD([[makeQuery(id+"F2.imprint","IMPRINT",EDGE,{"derivedFrom":sQuery(id+"F2.wireOp",EDGE,"E2.2.0.0")}),-1.0]])]});
            var Q33;
            Q33=makeQuery(id+"F2.imprint","IMPRINT",FACE,{"disambiguationData":[TD([[makeQuery(id+"F2.imprint","IMPRINT",EDGE,{"derivedFrom":sQuery(id+"F2.wireOp",EDGE,"E2.1.3.0")}),-1.0]])]});
            var Q34;
            Q34=makeQuery(id+"F2.imprint","IMPRINT",FACE,{"disambiguationData":[TD([[makeQuery(id+"F2.imprint","IMPRINT",EDGE,{"derivedFrom":sQuery(id+"F2.wireOp",EDGE,"E2.6.3.0")}),-1.0]])]});
            var Q35;
            Q35=makeQuery(id+"F2.imprint","IMPRINT",FACE,{"disambiguationData":[TD([[makeQuery(id+"F2.imprint","IMPRINT",EDGE,{"derivedFrom":sQuery(id+"F2.wireOp",EDGE,"E2.10.3.0")}),-1.0]])]});
            var Q36;
            Q36=makeQuery(id+"F2.imprint","IMPRINT",FACE,{"disambiguationData":[TD([[makeQuery(id+"F2.imprint","IMPRINT",EDGE,{"derivedFrom":sQuery(id+"F2.wireOp",EDGE,"E2.9.3.0")}),-1.0]])]});
            var Q37;
            Q37=makeQuery(id+"F2.imprint","IMPRINT",FACE,{"disambiguationData":[TD([[makeQuery(id+"F2.imprint","IMPRINT",EDGE,{"derivedFrom":sQuery(id+"F2.wireOp",EDGE,"E2.5.3.0")}),-1.0]])]});
            var Q38;
            Q38=makeQuery(id+"F2.imprint","IMPRINT",FACE,{"disambiguationData":[TD([[makeQuery(id+"F2.imprint","IMPRINT",EDGE,{"derivedFrom":sQuery(id+"F2.wireOp",EDGE,"E2.4.1.0")}),-1.0]])]});
            var Q39;
            Q39=makeQuery(id+"F2.imprint","IMPRINT",FACE,{"disambiguationData":[TD([[makeQuery(id+"F2.imprint","IMPRINT",EDGE,{"derivedFrom":sQuery(id+"F2.wireOp",EDGE,"E2.8.1.0")}),-1.0]])]});
            var Q40;
            Q40=makeQuery(id+"F2.imprint","IMPRINT",FACE,{"disambiguationData":[TD([[makeQuery(id+"F2.imprint","IMPRINT",EDGE,{"derivedFrom":sQuery(id+"F2.wireOp",EDGE,"E2.9.1.0")}),-1.0]])]});
            var Q41;
            Q41=makeQuery(id+"F2.imprint","IMPRINT",FACE,{"disambiguationData":[TD([[makeQuery(id+"F2.imprint","IMPRINT",EDGE,{"derivedFrom":sQuery(id+"F2.wireOp",EDGE,"E2.10.1.0")}),-1.0]])]});
            var Q42;
            Q42=makeQuery(id+"F2.imprint","IMPRINT",FACE,{"disambiguationData":[TD([[makeQuery(id+"F2.imprint","IMPRINT",EDGE,{"derivedFrom":sQuery(id+"F2.wireOp",EDGE,"E2.6.1.0")}),-1.0]])]});
            var Q43;
            Q43=makeQuery(id+"F2.imprint","IMPRINT",FACE,{"disambiguationData":[TD([[makeQuery(id+"F2.imprint","IMPRINT",EDGE,{"derivedFrom":sQuery(id+"F2.wireOp",EDGE,"E2.8.0.0")}),-1.0]])]});
            var Q44;
            Q44=makeQuery(id+"F2.imprint","IMPRINT",FACE,{"disambiguationData":[TD([[makeQuery(id+"F2.imprint","IMPRINT",EDGE,{"derivedFrom":sQuery(id+"F2.wireOp",EDGE,"E2.10.2.0")}),-1.0]])]});
            var Q45;
            Q45=makeQuery(id+"F2.imprint","IMPRINT",FACE,{"disambiguationData":[TD([[makeQuery(id+"F2.imprint","IMPRINT",EDGE,{"derivedFrom":sQuery(id+"F2.wireOp",EDGE,"E2.7.1.0")}),-1.0]])]});
            var Q46;
            Q46=makeQuery(id+"F2.imprint","IMPRINT",FACE,{"disambiguationData":[TD([[makeQuery(id+"F2.imprint","IMPRINT",EDGE,{"derivedFrom":sQuery(id+"F2.wireOp",EDGE,"E2.11.1.0")}),-1.0]])]});
            var Q47;
            Q47=makeQuery(id+"F2.imprint","IMPRINT",FACE,{"disambiguationData":[TD([[makeQuery(id+"F2.imprint","IMPRINT",EDGE,{"derivedFrom":sQuery(id+"F2.wireOp",EDGE,"E2.5.0.0")}),-1.0]])]});
            var Q48;
            Q48=makeQuery(id+"F2.imprint","IMPRINT",FACE,{"disambiguationData":[TD([[makeQuery(id+"F2.imprint","IMPRINT",EDGE,{"derivedFrom":sQuery(id+"F2.wireOp",EDGE,"E2.3.1.0")}),-1.0]])]});
            var Q49;
            Q49=makeQuery(id+"F2.imprint","IMPRINT",FACE,{"disambiguationData":[TD([[makeQuery(id+"F2.imprint","IMPRINT",EDGE,{"derivedFrom":sQuery(id+"F2.wireOp",EDGE,"E2.11.2.0")}),-1.0]])]});
            var Q50;
            Q50=makeQuery(id+"F2.imprint","IMPRINT",FACE,{"disambiguationData":[TD([[makeQuery(id+"F2.imprint","IMPRINT",EDGE,{"derivedFrom":sQuery(id+"F2.wireOp",EDGE,"E2.2.1.0")}),-1.0]])]});
            var Q51;
            Q51=makeQuery(id+"F2.imprint","IMPRINT",FACE,{"disambiguationData":[TD([[makeQuery(id+"F2.imprint","IMPRINT",EDGE,{"derivedFrom":sQuery(id+"F2.wireOp",EDGE,"E2.7.2.0")}),-1.0]])]});
            var Q52;
            Q52=makeQuery(id+"F2.imprint","IMPRINT",FACE,{"disambiguationData":[TD([[makeQuery(id+"F2.imprint","IMPRINT",EDGE,{"derivedFrom":sQuery(id+"F2.wireOp",EDGE,"E2.12.2.0")}),-1.0]])]});
            var Q53;
            Q53=makeQuery(id+"F2.imprint","IMPRINT",FACE,{"disambiguationData":[TD([[makeQuery(id+"F2.imprint","IMPRINT",EDGE,{"derivedFrom":sQuery(id+"F2.wireOp",EDGE,"E2.12.3.0")}),-1.0]])]});
            var Q54;
            Q54=makeQuery(id+"F2.imprint","IMPRINT",FACE,{"disambiguationData":[TD([[makeQuery(id+"F2.imprint","IMPRINT",EDGE,{"derivedFrom":sQuery(id+"F2.wireOp",EDGE,"E2.13.3.0")}),-1.0]])]});
            extrude(context, id + "F3", {"entities" : qUnion([Q0, Q1, Q2, Q3, Q4, Q5, Q6, Q7, Q8, Q9, Q10, Q11, Q12, Q13, Q14, Q15, Q16, Q17, Q18, Q19, Q20, Q21, Q22, Q23, Q24, Q25, Q26, Q27, Q28, Q29, Q30, Q31, Q32, Q33, Q34, Q35, Q36, Q37, Q38, Q39, Q40, Q41, Q42, Q43, Q44, Q45, Q46, Q47, Q48, Q49, Q50, Q51, Q52, Q53, Q54]), "operationType" : NewBodyOperationType.ADD, "depth" : 2.15 * mm, "offsetDistance" : 25 * mm});
        }
        {
            var Q0;
            Q0=makeQuery(id+"F3.opExtrude","CAP_FACE",FACE,{"disambiguationData":[OSD([sQuery(id+"F2.wireOp",EDGE,"E2.3.1.0"),sQuery(id+"F2.wireOp",EDGE,"E2.3.1.1"),sQuery(id+"F2.wireOp",EDGE,"E2.3.1.2"),sQuery(id+"F2.wireOp",EDGE,"E2.3.1.4")])],"isStart":false});
            var sketch = newSketch(context, id + "F4", { "sketchPlane" : qUnion([Q0])});
            skText(sketch, "E3", { "text": "P", "fontName": "OpenSans-Regular.ttf"});
            const initialGuessF4  = {"E3": [0.06478, 0.01069, 1, 0, 0.00742]};
            skSetInitialGuess(sketch, initialGuessF4);
            skSolve(sketch);
        }
        {
            var Q0;
            Q0=makeQuery(id+"F4.imprint","IMPRINT",FACE,{"disambiguationData":[TD([[makeQuery(id+"F4.imprint","IMPRINT",EDGE,{"derivedFrom":sQuery(id+"F4.wireOp",EDGE,"E3.sketch_text.stroke-0")}),-1.0]])]});
            extrude(context, id + "F5", {"entities" : qUnion([Q0]), "operationType" : NewBodyOperationType.REMOVE, "oppositeDirection" : true, "depth" : 0.1 * mm, "offsetDistance" : 25 * mm});
        }
        {
            var Q0;
            Q0=makeQuery(id+"F3.opExtrude","CAP_FACE",FACE,{"disambiguationData":[OSD([sQuery(id+"F2.wireOp",EDGE,"E2.4.1.0"),sQuery(id+"F2.wireOp",EDGE,"E2.4.1.1"),sQuery(id+"F2.wireOp",EDGE,"E2.4.1.2"),sQuery(id+"F2.wireOp",EDGE,"E2.4.1.4")])],"isStart":false});
            var sketch = newSketch(context, id + "F6", { "sketchPlane" : qUnion([Q0])});
            skText(sketch, "E4", { "text": "O", "fontName": "OpenSans-Regular.ttf"});
            const initialGuessF6  = {"E4": [0.04532, 0.01002, 1, 0, 0.00818]};
            skSetInitialGuess(sketch, initialGuessF6);
            skSolve(sketch);
        }
        {
            var Q0;
            Q0=makeQuery(id+"F6.imprint","IMPRINT",FACE,{"disambiguationData":[TD([[makeQuery(id+"F6.imprint","IMPRINT",EDGE,{"derivedFrom":sQuery(id+"F6.wireOp",EDGE,"E4.sketch_text.stroke-0")}),-1.0]])]});
            extrude(context, id + "F7", {"entities" : qUnion([Q0]), "operationType" : NewBodyOperationType.REMOVE, "oppositeDirection" : true, "depth" : 0.1 * mm, "offsetDistance" : 25 * mm});
        }
        {
            var Q0;
            Q0=makeQuery(id+"F3.opExtrude","CAP_FACE",FACE,{"disambiguationData":[OSD([sQuery(id+"F2.wireOp",EDGE,"E2.4.2.0"),sQuery(id+"F2.wireOp",EDGE,"E2.4.2.1"),sQuery(id+"F2.wireOp",EDGE,"E2.4.2.2"),sQuery(id+"F2.wireOp",EDGE,"E2.4.2.4")])],"isStart":false});
            var sketch = newSketch(context, id + "F8", { "sketchPlane" : qUnion([Q0])});
            skText(sketch, "E5", { "text": "L", "fontName": "OpenSans-Regular.ttf"});
            const initialGuessF8  = {"E5": [0.05123, -0.00872, 1, 0, 0.00872]};
            skSetInitialGuess(sketch, initialGuessF8);
            skSolve(sketch);
        }
        {
            var Q0;
            Q0=makeQuery(id+"F8.imprint","IMPRINT",FACE,{"disambiguationData":[TD([[makeQuery(id+"F8.imprint","IMPRINT",EDGE,{"derivedFrom":sQuery(id+"F8.wireOp",EDGE,"E5.sketch_text.stroke-0")}),-1.0]])]});
            extrude(context, id + "F9", {"entities" : qUnion([Q0]), "operationType" : NewBodyOperationType.REMOVE, "oppositeDirection" : true, "depth" : 0.1 * mm, "offsetDistance" : 25 * mm});
        }
        {
            var Q0;
            Q0=makeQuery(id+"F3.opExtrude","CAP_FACE",FACE,{"disambiguationData":[OSD([sQuery(id+"F2.wireOp",EDGE,"E2.5.2.0"),sQuery(id+"F2.wireOp",EDGE,"E2.5.2.1"),sQuery(id+"F2.wireOp",EDGE,"E2.5.2.2"),sQuery(id+"F2.wireOp",EDGE,"E2.5.2.4")])],"isStart":false});
            var sketch = newSketch(context, id + "F10", { "sketchPlane" : qUnion([Q0])});
            skText(sketch, "E6", { "text": "K", "fontName": "OpenSans-Regular.ttf"});
            const initialGuessF10  = {"E6": [0.03173, -0.0089, 1, 0, 0.0089]};
            skSetInitialGuess(sketch, initialGuessF10);
            skSolve(sketch);
        }
        {
            var Q0;
            Q0=makeQuery(id+"F10.imprint","IMPRINT",FACE,{"disambiguationData":[TD([[makeQuery(id+"F10.imprint","IMPRINT",EDGE,{"derivedFrom":sQuery(id+"F10.wireOp",EDGE,"E6.sketch_text.stroke-0")}),-1.0]])]});
            extrude(context, id + "F11", {"entities" : qUnion([Q0]), "operationType" : NewBodyOperationType.REMOVE, "oppositeDirection" : true, "depth" : 0.1 * mm, "offsetDistance" : 25 * mm});
        }
        {
            var Q0;
            Q0=makeQuery(id+"F1.opExtrude","CAP_FACE",FACE,{"disambiguationData":[OSD([sQuery(id+"F0.wireOp",EDGE,"E0.bottom"),sQuery(id+"F0.wireOp",EDGE,"E0.top"),sQuery(id+"F0.wireOp",EDGE,"E0.left"),sQuery(id+"F0.wireOp",EDGE,"E0.right")])],"isStart":false});
            var sketch = newSketch(context, id + "F12", { "sketchPlane" : qUnion([Q0])});
            skSolve(sketch);
        }
        {
            var Q0;
            Q0=makeQuery(id+"F12.imprint","IMPRINT",FACE,{"disambiguationData":[TD([[makeQuery(id+"F12.imprint","IMPRINT",EDGE,{"derivedFrom":makeQuery(id+"F1.opExtrude","CAP_EDGE",EDGE,{"disambiguationData":[OSD([sQuery(id+"F0.wireOp",EDGE,"E0.bottom")])],"isStart":false})}),-1.0]])]});
            var sketch = newSketch(context, id + "F13", { "sketchPlane" : qUnion([Q0])});
            skLineSegment(sketch, "E7.left", {"start": v(-134.7, -58) * mm, "end": v(-134.7, -33) * mm});
            skLineSegment(sketch, "E7.right", {"start": v(134.7, -58) * mm, "end": v(134.7, -33) * mm});
            skPoint(sketch, "E7.middle", {"position": v(0, -45.5) * mm});
            skLineSegment(sketch, "E8", {"start": v(134.7, -58) * mm, "end": v(-134.7, -58) * mm});
            skLineSegment(sketch, "E9", {"start": v(134.7, -33) * mm, "end": v(-134.7, -33) * mm});
            skSolve(sketch);
        }
        {
            var Q0;
            Q0=makeQuery(id+"F13.imprint","IMPRINT",FACE,{"disambiguationData":[TD([[makeQuery(id+"F13.imprint","IMPRINT",EDGE,{"derivedFrom":sQuery(id+"F13.wireOp",EDGE,"E7.left")}),-1.0]])]});
            extrude(context, id + "F14", {"entities" : qUnion([Q0]), "operationType" : NewBodyOperationType.ADD, "depth" : 13.25 * mm, "offsetDistance" : 25 * mm});
        }
    });
